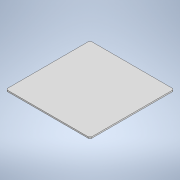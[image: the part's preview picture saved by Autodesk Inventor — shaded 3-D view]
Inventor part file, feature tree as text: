
AUTODESK INVENTOR PART (.ipt)
format: ipt  version: 2020 (Build 240168000, 168)  size: 97,280 bytes
history: native  units: mm
features: extrude x1, chamfer x1, sketch x1
ambient origin geometry x8: Origin, YZ Plane, XZ Plane, XY Plane, X Axis, Y Axis, Z Axis, Center Point
bodies: Solid1 (feature_tree)
feature tree (3):
  extrude  "Extrusion1"  Depth=125.0mm
  chamfer  "Chamfer1"  Distance=2.0mm
  sketch  "Sketch1"  dims[d0=125.0mm d1=125.0mm d2=2.0mm d3=0.0mm d4=2.0mm d5=2.0mm d6=45.0deg]
